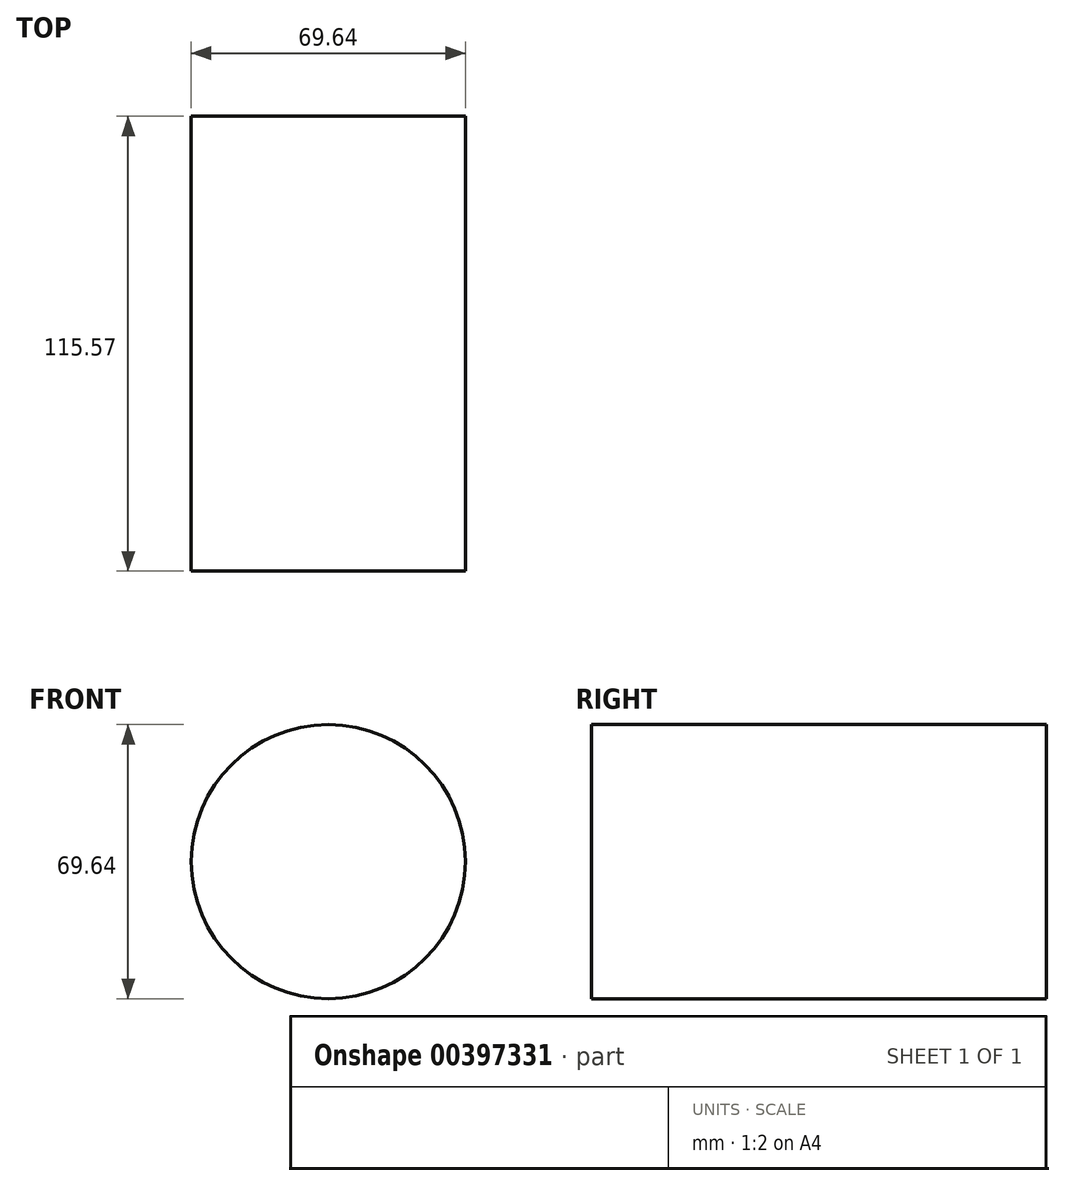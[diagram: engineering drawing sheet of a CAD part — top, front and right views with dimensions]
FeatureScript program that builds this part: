
annotation { "Feature Type Name" : "Feature", "Feature Type Description" : "" }
export const myFeature = defineFeature(function(context is Context, id is Id, definition is map)
    precondition{}
    {
        {
            var Q0;
            Q0=qCreatedBy(makeId("Front.planeOp"),FACE);
            var sketch = newSketch(context, id + "F0", { "sketchPlane" : qUnion([Q0])});
            skCircle(sketch, "E0", {"center": v(-13.76, 31.99) * mm, "radius": 34.82 * mm});
            skSolve(sketch);
        }
        {
            var Q0;
            Q0=makeQuery(id+"F0.imprint","IMPRINT",FACE,{"disambiguationData":[TD([[makeQuery(id+"F0.imprint","IMPRINT",EDGE,{"derivedFrom":sQuery(id+"F0.wireOp",EDGE,"E0")}),1.0]])]});
            extrude(context, id + "F1", {"entities" : qUnion([Q0]), "depth" : 115.57 * mm});
        }
    });
